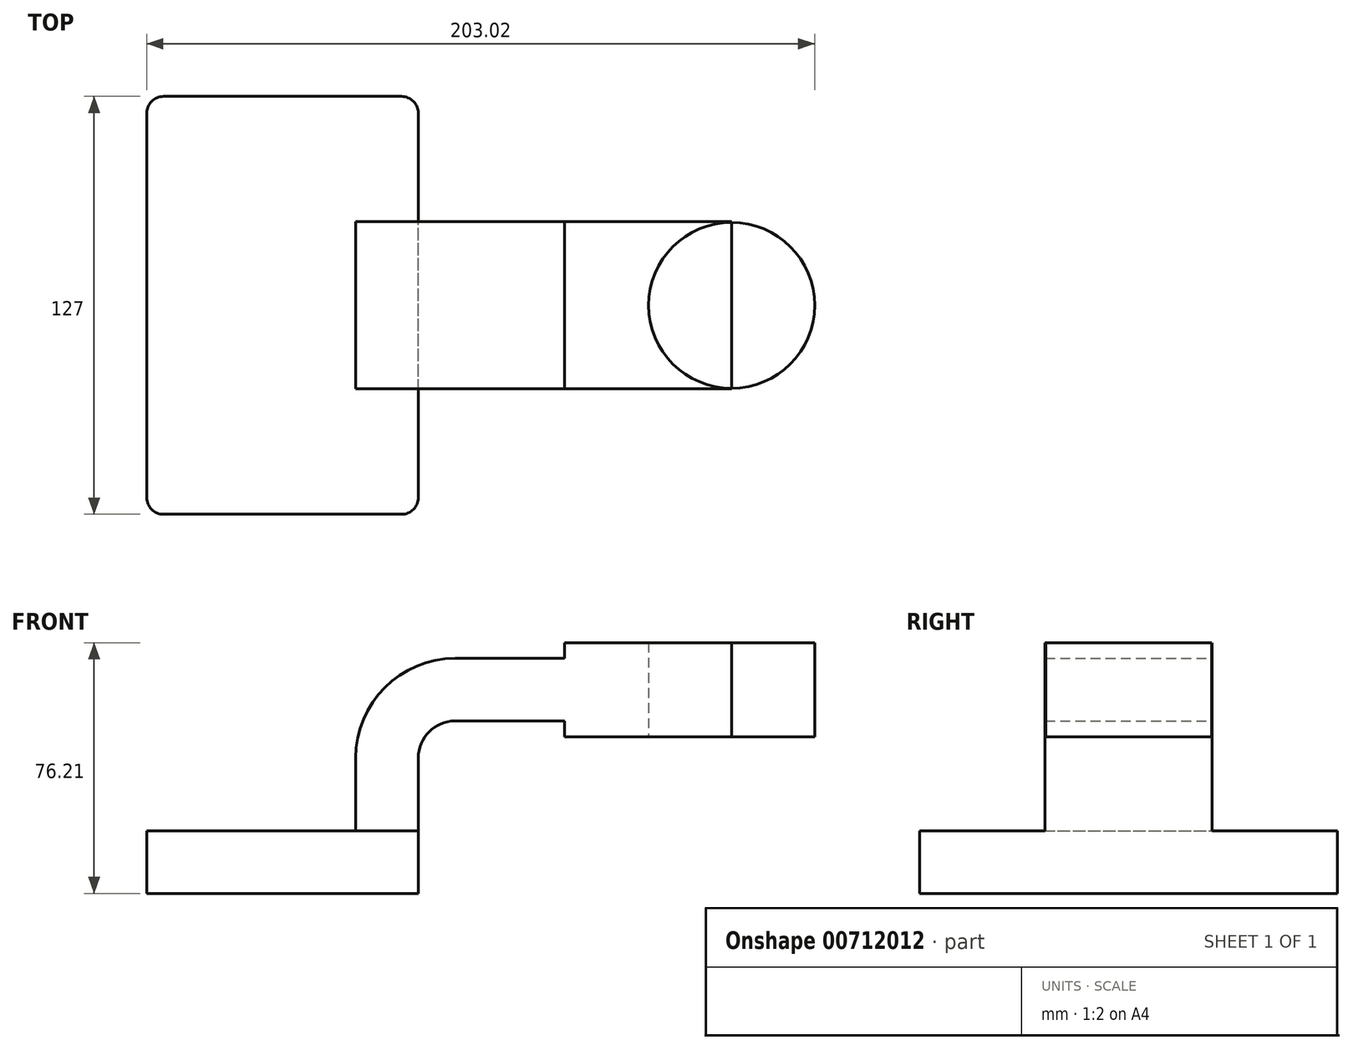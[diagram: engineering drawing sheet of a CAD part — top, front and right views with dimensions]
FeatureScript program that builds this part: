
annotation { "Feature Type Name" : "Feature", "Feature Type Description" : "" }
export const myFeature = defineFeature(function(context is Context, id is Id, definition is map)
    precondition{}
    {
        {
            var Q0;
            Q0=qCreatedBy(makeId("Front.planeOp"),FACE);
            var sketch = newSketch(context, id + "F0", { "sketchPlane" : qUnion([Q0])});
            skLineSegment(sketch, "E0.bottom", {"start": v(-41.28, 9.52) * mm, "end": v(41.28, 9.53) * mm});
            skLineSegment(sketch, "E0.top", {"start": v(-41.28, -9.53) * mm, "end": v(41.28, -9.53) * mm});
            skLineSegment(sketch, "E0.left", {"start": v(-41.28, 9.52) * mm, "end": v(-41.28, -9.53) * mm});
            skLineSegment(sketch, "E0.right", {"start": v(41.27, 9.53) * mm, "end": v(41.28, -9.52) * mm});
            skPoint(sketch, "E0.middle", {"position": v(0, 0) * mm});
            skLineSegment(sketch, "E1.bottom", {"start": v(136.53, 38.1) * mm, "end": v(85.72, 38.1) * mm});
            skLineSegment(sketch, "E1.top", {"start": v(136.53, 66.68) * mm, "end": v(85.72, 66.68) * mm});
            skLineSegment(sketch, "E1.left", {"start": v(136.53, 38.1) * mm, "end": v(136.53, 66.68) * mm});
            skLineSegment(sketch, "E1.right", {"start": v(85.72, 38.1) * mm, "end": v(85.72, 66.67) * mm});
            skPoint(sketch, "E1.middle", {"position": v(111.12, 52.39) * mm});
            skLineSegment(sketch, "E2", {"start": v(41.27, 9.53) * mm, "end": v(41.27, 31.65) * mm});
            skArc(sketch, "E3", {"start": v(41.27, 31.65) * mm, "mid": v(44.56, 39.59) * mm, "end": v(52.5, 42.88) * mm});
            skLineSegment(sketch, "E4", {"start": v(52.5, 42.88) * mm, "end": v(111.3, 42.88) * mm});
            skLineSegment(sketch, "E5.0", {"start": v(52.5, 61.93) * mm, "end": v(111.3, 61.93) * mm});
            skArc(sketch, "E5.1", {"start": v(22.22, 31.65) * mm, "mid": v(31.1, 53.06) * mm, "end": v(52.5, 61.93) * mm});
            skLineSegment(sketch, "E5.2", {"start": v(22.22, 9.53) * mm, "end": v(22.22, 31.65) * mm});
            skLineSegment(sketch, "E6", {"start": v(111.3, 38.1) * mm, "end": v(111.3, 66.67) * mm});
            skFitSpline(sketch, "E7", {"points": [v(-41.28, 9.52) * mm, v(52.5, 61.93) * mm], "startDerivative": vector(12.66, 97.42) * mm, "endDerivative": vector(128.17, -1.17) * mm});
            skSolve(sketch);
        }
        {
            var Q0;
            Q0=makeQuery(id+"F0.imprint","IMPRINT",FACE,{"disambiguationData":[TD([[makeQuery(id+"F0.imprint","IMPRINT",EDGE,{"derivedFrom":sQuery(id+"F0.wireOp",EDGE,"E0.top")}),1.0]])]});
            extrude(context, id + "F1", {"entities" : qUnion([Q0]), "endBound" : BoundingType.SYMMETRIC, "depth" : 127 * mm, "offsetDistance" : 25.4 * mm});
        }
        {
            var Q0;
            {var subQ4=sQuery(id+"F0.wireOp",EDGE,"E1.left");Q0=makeQuery(id+"F0.imprint","IMPRINT",FACE,{"disambiguationData":[TD([[makeQuery(id+"F0.imprint","IMPRINT",EDGE,{"derivedFrom":subQ4}),1.0]])]});}
            var Q1;
            {var subQ0=sQuery(id+"F0.wireOp",EDGE,"E1.right");var subQ1=sQuery(id+"F0.wireOp",EDGE,"E1.top");var subQ2=makeQuery(id+"F0.imprint","INTERSECT",VERTEX,{"derivedFrom":[subQ1,subQ0]});Q1=makeQuery(id+"F0.imprint","IMPRINT",FACE,{"disambiguationData":[TD([[makeQuery(id+"F0.imprint","IMPRINT",EDGE,{"disambiguationData":[TD([[subQ2,1.0]])],"derivedFrom":subQ1}),1.0]])]});}
            var Q2;
            {var subQ0=sQuery(id+"F0.wireOp",EDGE,"E4");var subQ1=sQuery(id+"F0.wireOp",EDGE,"E1.right");var subQ2=makeQuery(id+"F0.imprint","INTERSECT",VERTEX,{"derivedFrom":[subQ1,subQ0]});Q2=makeQuery(id+"F0.imprint","IMPRINT",FACE,{"disambiguationData":[TD([[makeQuery(id+"F0.imprint","IMPRINT",EDGE,{"disambiguationData":[TD([[subQ2,-1.0]])],"derivedFrom":subQ1}),-1.0]])]});}
            var Q3;
            {var subQ0=sQuery(id+"F0.wireOp",EDGE,"E1.right");var subQ1=sQuery(id+"F0.wireOp",EDGE,"E1.bottom");var subQ2=makeQuery(id+"F0.imprint","INTERSECT",VERTEX,{"derivedFrom":[subQ1,subQ0]});Q3=makeQuery(id+"F0.imprint","IMPRINT",FACE,{"disambiguationData":[TD([[makeQuery(id+"F0.imprint","IMPRINT",EDGE,{"disambiguationData":[TD([[subQ2,1.0]])],"derivedFrom":subQ1}),-1.0]])]});}
            var Q4;
            {var subQ1=sQuery(id+"F0.wireOp",EDGE,"E2");Q4=makeQuery(id+"F0.imprint","IMPRINT",FACE,{"disambiguationData":[TD([[makeQuery(id+"F0.imprint","IMPRINT",EDGE,{"derivedFrom":subQ1}),1.0]])]});}
            extrude(context, id + "F2", {"entities" : qUnion([Q0, Q1, Q2, Q3, Q4]), "operationType" : NewBodyOperationType.ADD, "endBound" : BoundingType.SYMMETRIC, "depth" : 50.8 * mm, "offsetDistance" : 25.4 * mm});
        }
        {
            var Q0;
            Q0=makeQuery(id+"F0.imprint","IMPRINT",FACE,{"disambiguationData":[TD([[makeQuery(id+"F0.imprint","IMPRINT",EDGE,{"derivedFrom":sQuery(id+"F0.wireOp",EDGE,"E5.1")}),1.0]])]});
            extrude(context, id + "F3", {"entities" : qUnion([Q0]), "operationType" : NewBodyOperationType.ADD, "endBound" : BoundingType.SYMMETRIC, "depth" : 15.88 * mm, "offsetDistance" : 25.4 * mm});
        }
        {
            var Q0;
            {var subQ4=sQuery(id+"F0.wireOp",EDGE,"E1.left");Q0=makeQuery(id+"F0.imprint","IMPRINT",FACE,{"disambiguationData":[TD([[makeQuery(id+"F0.imprint","IMPRINT",EDGE,{"derivedFrom":subQ4}),1.0]])]});}
            var Q1;
            Q1=sQuery(id+"F0.wireOp",EDGE,"E1.left");
            revolve(context, id + "F4", {"surfaceOperationType" : NewSurfaceOperationType.NEW, "entities" : qUnion([Q0]), "axis" : qUnion([Q1]), "revolveType" : RevolveType.FULL});
        }
        {
            var Q0;
            Q0=makeQuery(id+"F1.opExtrude","CAP_EDGE",EDGE,{"disambiguationData":[OSD([sQuery(id+"F0.wireOp",EDGE,"E0.right")])],"isStart":false});
            var Q1;
            Q1=makeQuery(id+"F1.opExtrude","CAP_EDGE",EDGE,{"disambiguationData":[OSD([sQuery(id+"F0.wireOp",EDGE,"E0.left")])],"isStart":false});
            var Q2;
            Q2=makeQuery(id+"F1.opExtrude","CAP_EDGE",EDGE,{"disambiguationData":[OSD([sQuery(id+"F0.wireOp",EDGE,"E0.left")])],"isStart":true});
            var Q3;
            Q3=makeQuery(id+"F1.opExtrude","CAP_EDGE",EDGE,{"disambiguationData":[OSD([sQuery(id+"F0.wireOp",EDGE,"E0.right")])],"isStart":true});
            fillet(context, id + "F5", {"entities" : qUnion([Q0, Q1, Q2, Q3]), "radius" : 5.08 * mm, "tangentPropagation" : true, "allowEdgeOverflow" : false});
        }
    });
